# Revit family: PRD_AR_MxrTps_HybridKitchenFittings_F5LME001_F5LME002
name_source: partatom
category: Plumbing Fixtures
units: mm (PartAtom-declared; Revit-internal decimal feet)

## family parameters
Always vertical = Yes
Cut with Voids When Loaded = No
OmniClass Number = 23.45.55.17
OmniClass Title = Mixing Faucets
Part Type = Normal
Room Calculation Point = No
Round Connector Dimension = Use Diameter
Shared = No
Work Plane-Based = No

## types (2) — shared parameters
AccentColour = none
AssetType = Fixed
BodyMaterial = PRD_AR_StainlessSteel_Brushed
Category = Pr_40_20_87_55, Mixer taps
CloseOffRating = 0.0 Pa
DiameterNominal = 15 mm
DurationUnit = year
FaucetFunction = Mixed
FaucetOperation = LeverHandle
FaucetType = Pillar
FunctionalPrinciple = manual
HygieneFlushing = prepared
IfcExportAs = IfcValveType
IfcExportType = FAUCET
LockingMechanism = Top section, non-ceramic
Manufacturer = KWC Group AG
ManufacturerName = KWC Group AG
ManufacturerURL = www.kwc.com
Material = stainless steel
MaterialFitting = stainless steel
MinimumFlowPressure = 1 bar
NBSDescription = Taps and water supply fittings for sinks
NBSReference = 45-35-70/345
NominalHeight = 392 mm  [stored 1.28609 ft]
Pop-upWasteSet = no
PowerConsumption = 1.5 Voltampere
PowerSupplyConnection = 6,75 / 12 V DC / A3000 open
ProductInformation = http://pim.kwc.com
ProtectiveSystemIP = IP 59K
Shape = Pillar tap
Size = 15
Spout = rotating, top
Status = New
SurfaceFinishFitting = brushed
TailorMade = no
TemperatureLimit = yes
TestPressure = 0.0 Pa
ThermalDisinfection = yes
TypeOfMixing = yes
TypeOfMounting = tap hole
TypeOfOperation = manual operation
TypeOfTap = pillar tap
URL = www.kwc.com
Uniclass2015Code = Pr_40_20_87_55
Uniclass2015Title = Mixer taps
Uniclass2015Version = Products v1.32
ValveMechanism = OTHER
ValveOperation = LEVER
ValvePattern = STRAIGHT_3_PORT
Version = 1
WarrantyDurationUnit = year
WaterConnection = hose (gland nut)
WithFilter = yes
WithRosettesOrCoverPlate = no
WorkingPressure = 0.0 Pa
zero-valued in all types: Default Elevation, FlowCoefficient, NominalDepth, NominalWidth

## per-type parameters (varying)
| type | BIMObjectName | Depressurised | Description | Features | ModelNumber | Name | VolumeFlowRate |
| F5LME001 | PRD_AR_MixerTaps_HybridKitchenFittings_F5LME001 | no | F5LME hybrid kitchen fitting DN 15 as pillar mixer with swivelling spout, can be locked in the centre position. Adjustable swivel ranges of 50°, 120° and 360°. For connection to hot water and cold water via hoses with strainers. Single lever mixer with mixer cartridge with ceramic disc technology and adjustable, turn-proof temperature stop. Alternative activation using hand reflection via an opto-electronic sensor for time-controlled water release with preset mixing water temperature. Mixer cartridge, solenoid valve and sensor with control electronics in all-metal housing, brushed stainless steel. Laminar jet controller with integrated flow rate controller (8.0 l/min). Projection 220 mm. Activated water hygiene flushing 24 hours after last activation, safety switch-off for continuous reflection and saving of statistical data. With option for parametrisation and communication via optional, bidirectional remote control. Optionally for battery operation with battery compartment including 6 V lithium battery (CR-P2) per fitting for installation under the kitchen sink or for separate power supply via 6.75 V/12 V DC power supply unit or AQUA 3000 open system accessories. | For connection to hot water and cold water via hoses with strainers. With integrated flow rate controller (8.0 l/min). Projection 220 mm. | 2030061048 | F5LME Hybrid kitchen fitting F5LME001 | 0.13 l/s at 3 bar |
| F5LME002 | PRD_AR_MixerTaps_HybridKitchenFittings_F5LME002 | yes | F5LME hybrid kitchen fitting DN 15 as pillar mixer with swivelling spout, can be locked in the centre position. Adjustable swivel ranges of 50°, 120° and 360°. To the connection via hoses in open undercounter boilers. Single lever mixer with mixer cartridge with ceramic disc technology and adjustable, turn-proof temperature stop. Alternative activation using hand reflection via an opto-electronic sensor for time-controlled water release with preset mixing water temperature. Mixer cartridge, solenoid valve and sensor with control electronics in all-metal housing, brushed stainless steel. With beam shaper. Projection 220 mm. Activated water hygiene flushing 24 hours after last activation, safety switch-off for continuous reflection and saving of statistical data. With option for parametrisation and communication via optional, bidirectional remote control. Optionally for battery operation with battery compartment including 6 V lithium battery (CR-P2) per fitting for installation under the kitchen sink or for separate power supply via 6.75 V/12 V DC power supply unit or AQUA 3000 open system accessories. | To the connection via hoses in open undercounter boilers. Projection 220 mm. | 2030061065 | F5LME Hybrid kitchen fitting for hot water heater F5LME002 | 0.08 l/s at 3 bar |

note: column(s) folded — value = type name in every type: Model, ModelReference

note: [stored X ft] marks values corroborated as IEEE doubles in the binary element streams (Revit-internal decimal feet)

## geometry (parser evidence)
native form markers: Sweep x6
no freeform markers — native parametric forms only
